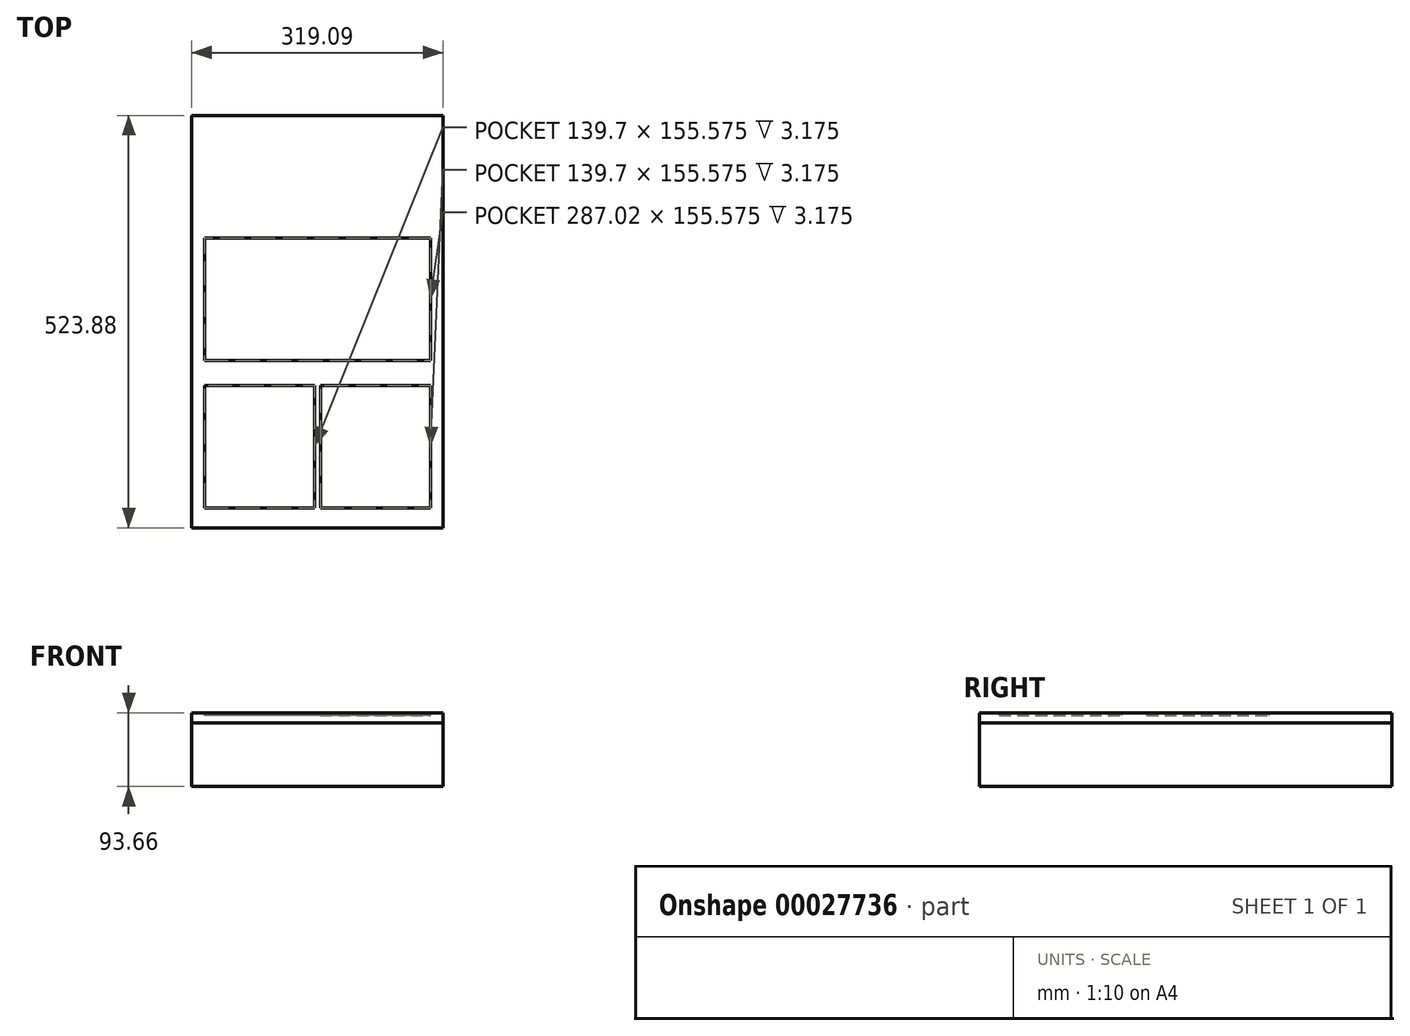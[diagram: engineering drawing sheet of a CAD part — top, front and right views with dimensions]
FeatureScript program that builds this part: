
annotation { "Feature Type Name" : "Feature", "Feature Type Description" : "" }
export const myFeature = defineFeature(function(context is Context, id is Id, definition is map)
    precondition{}
    {
        {
            var Q0;
            Q0=qCreatedBy(makeId("Top.planeOp"),FACE);
            var sketch = newSketch(context, id + "F0", { "sketchPlane" : qUnion([Q0])});
            skLineSegment(sketch, "E0.bottom", {"start": v(0, 0) * mm, "end": v(319.09, 0) * mm});
            skLineSegment(sketch, "E0.top", {"start": v(0, 523.88) * mm, "end": v(319.09, 523.88) * mm});
            skLineSegment(sketch, "E0.left", {"start": v(0, 0) * mm, "end": v(0, 523.88) * mm});
            skLineSegment(sketch, "E0.right", {"start": v(319.09, 0) * mm, "end": v(319.09, 523.88) * mm});
            skSolve(sketch);
        }
        {
            var Q0;
            Q0 = qSketchRegion(id + "F0", true);
            extrude(context, id + "F1", {"entities" : qUnion([Q0]), "depth" : 80.96 * mm});
        }
        {
            var Q0;
            Q0=makeQuery(id+"F1.opExtrude","CAP_FACE",FACE,{"disambiguationData":[OSD([sQuery(id+"F0.wireOp",EDGE,"E0.bottom"),sQuery(id+"F0.wireOp",EDGE,"E0.top"),sQuery(id+"F0.wireOp",EDGE,"E0.left"),sQuery(id+"F0.wireOp",EDGE,"E0.right")])],"isStart":false});
            var sketch = newSketch(context, id + "F2", { "sketchPlane" : qUnion([Q0])});
            skLineSegment(sketch, "E1", {"start": v(30.16, 0) * mm, "end": v(30.16, 523.88) * mm});
            skLineSegment(sketch, "E2", {"start": v(79.38, 0) * mm, "end": v(79.38, 523.88) * mm});
            skLineSegment(sketch, "E3", {"start": v(128.2, 523.88) * mm, "end": v(128.2, 0) * mm});
            skLineSegment(sketch, "E4", {"start": v(159.54, 523.88) * mm, "end": v(159.54, 0) * mm, "construction": true});
            skLineSegment(sketch, "E5.MirrorCS", {"start": v(190.9, 523.88) * mm, "end": v(190.9, 0) * mm});
            skLineSegment(sketch, "E6.MirrorCS", {"start": v(239.71, 0) * mm, "end": v(239.71, 523.88) * mm});
            skLineSegment(sketch, "E7.MirrorCS", {"start": v(288.93, 0) * mm, "end": v(288.92, 523.88) * mm});
            skLineSegment(sketch, "E8.bottom", {"start": v(16.03, 0) * mm, "end": v(303.05, 0) * mm, "construction": true});
            skLineSegment(sketch, "E8.top", {"start": v(16.03, 373.38) * mm, "end": v(303.05, 373.38) * mm, "construction": true});
            skLineSegment(sketch, "E8.left", {"start": v(16.03, 0) * mm, "end": v(16.03, 373.38) * mm, "construction": true});
            skLineSegment(sketch, "E8.right", {"start": v(303.05, 0) * mm, "end": v(303.05, 373.38) * mm, "construction": true});
            skSolve(sketch);
        }
        {
            var Q0;
            {var subQ2=sQuery(id+"F2.wireOp",EDGE,"E1");Q0=makeQuery(id+"F2.imprint","IMPRINT",FACE,{"disambiguationData":[TD([[makeQuery(id+"F2.imprint","IMPRINT",EDGE,{"derivedFrom":subQ2}),-1.0]])]});}
            var sketch = newSketch(context, id + "F3", { "sketchPlane" : qUnion([Q0])});
            skLineSegment(sketch, "E9.bottom", {"start": v(0, 523.88) * mm, "end": v(319.09, 523.88) * mm});
            skLineSegment(sketch, "E9.top", {"start": v(0, 0) * mm, "end": v(319.09, 0) * mm});
            skLineSegment(sketch, "E9.left", {"start": v(0, 523.88) * mm, "end": v(0, 0) * mm});
            skLineSegment(sketch, "E9.right", {"start": v(319.09, 523.88) * mm, "end": v(319.09, 0) * mm});
            skSolve(sketch);
        }
        {
            var Q0;
            Q0 = qSketchRegion(id + "F3", true);
            extrude(context, id + "F4", {"entities" : qUnion([Q0]), "depth" : 12.7 * mm});
        }
        {
            var Q0;
            Q0=makeQuery(id+"F4.opExtrude","CAP_FACE",FACE,{"disambiguationData":[OSD([sQuery(id+"F3.wireOp",EDGE,"E9.bottom"),sQuery(id+"F3.wireOp",EDGE,"E9.top"),sQuery(id+"F3.wireOp",EDGE,"E9.left"),sQuery(id+"F3.wireOp",EDGE,"E9.right")])],"isStart":false});
            var sketch = newSketch(context, id + "F5", { "sketchPlane" : qUnion([Q0])});
            skLineSegment(sketch, "E10.bottom", {"start": v(16.03, 373.38) * mm, "end": v(303.05, 373.38) * mm, "construction": true});
            skLineSegment(sketch, "E10.top", {"start": v(16.03, 0) * mm, "end": v(303.05, 0) * mm, "construction": true});
            skLineSegment(sketch, "E10.left", {"start": v(16.03, 373.38) * mm, "end": v(16.03, 0) * mm, "construction": true});
            skLineSegment(sketch, "E10.right", {"start": v(303.05, 373.38) * mm, "end": v(303.05, 0) * mm, "construction": true});
            skLineSegment(sketch, "E11.bottom", {"start": v(155.73, 25.4) * mm, "end": v(16.03, 25.4) * mm});
            skLineSegment(sketch, "E11.top", {"start": v(155.73, 180.97) * mm, "end": v(16.03, 180.97) * mm});
            skLineSegment(sketch, "E11.left", {"start": v(155.73, 25.4) * mm, "end": v(155.73, 180.97) * mm});
            skLineSegment(sketch, "E11.right", {"start": v(16.03, 25.4) * mm, "end": v(16.03, 180.97) * mm});
            skLineSegment(sketch, "E12", {"start": v(159.54, 373.38) * mm, "end": v(159.54, 0) * mm, "construction": true});
            skLineSegment(sketch, "E13.MirrorCS", {"start": v(163.35, 25.4) * mm, "end": v(303.05, 25.4) * mm});
            skLineSegment(sketch, "E14.MirrorCS", {"start": v(163.35, 180.97) * mm, "end": v(303.05, 180.98) * mm});
            skLineSegment(sketch, "E15.MirrorCS", {"start": v(303.05, 25.4) * mm, "end": v(303.05, 180.97) * mm});
            skLineSegment(sketch, "E16.MirrorCS", {"start": v(163.35, 25.4) * mm, "end": v(163.35, 180.97) * mm});
            skLineSegment(sketch, "E17.0.1.0", {"start": v(303.05, 212.73) * mm, "end": v(303.05, 368.3) * mm});
            skLineSegment(sketch, "E17.0.1.4", {"start": v(16.03, 212.73) * mm, "end": v(16.03, 368.3) * mm});
            skLineSegment(sketch, "E17.0.1.6", {"start": v(155.73, 368.3) * mm, "end": v(16.03, 368.3) * mm});
            skLineSegment(sketch, "E17.0.1.7", {"start": v(155.73, 212.72) * mm, "end": v(16.03, 212.72) * mm});
            skLineSegment(sketch, "E17.direction1", {"start": v(303.05, 25.4) * mm, "end": v(328.45, 25.4) * mm, "construction": true});
            skLineSegment(sketch, "E17.direction2", {"start": v(303.05, 25.4) * mm, "end": v(303.05, 212.73) * mm, "construction": true});
            skLineSegment(sketch, "E18", {"start": v(155.73, 212.72) * mm, "end": v(303.05, 212.73) * mm});
            skLineSegment(sketch, "E19", {"start": v(155.73, 368.3) * mm, "end": v(303.05, 368.3) * mm});
            skSolve(sketch);
        }
        {
            var Q0;
            Q0=makeQuery(id+"F5.imprint","IMPRINT",FACE,{"disambiguationData":[TD([[makeQuery(id+"F5.imprint","IMPRINT",EDGE,{"derivedFrom":sQuery(id+"F5.wireOp",EDGE,"E17.0.1.3")}),1.0]])]});
            var Q1;
            Q1=makeQuery(id+"F5.imprint","IMPRINT",FACE,{"disambiguationData":[TD([[makeQuery(id+"F5.imprint","IMPRINT",EDGE,{"derivedFrom":sQuery(id+"F5.wireOp",EDGE,"E17.0.1.0")}),1.0]])]});
            var Q2;
            Q2=makeQuery(id+"F5.imprint","IMPRINT",FACE,{"disambiguationData":[TD([[makeQuery(id+"F5.imprint","IMPRINT",EDGE,{"derivedFrom":sQuery(id+"F5.wireOp",EDGE,"E13.MirrorCS")}),1.0]])]});
            var Q3;
            Q3=makeQuery(id+"F5.imprint","IMPRINT",FACE,{"disambiguationData":[TD([[makeQuery(id+"F5.imprint","IMPRINT",EDGE,{"derivedFrom":sQuery(id+"F5.wireOp",EDGE,"E11.bottom")}),-1.0]])]});
            extrude(context, id + "F6", {"entities" : qUnion([Q0, Q1, Q2, Q3]), "operationType" : NewBodyOperationType.REMOVE, "oppositeDirection" : true, "depth" : 3.17 * mm});
        }
    });
